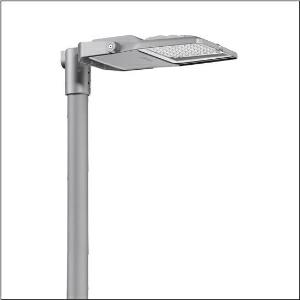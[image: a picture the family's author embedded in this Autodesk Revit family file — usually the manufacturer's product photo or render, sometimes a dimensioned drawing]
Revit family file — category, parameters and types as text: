
# Revit family: floodlight_fl_21_mini___pl33t_5xa7775d2f3a_2fb5
name_source: partatom
category: Lighting Fixtures
units: mm (PartAtom-declared; Revit-internal decimal feet)

## family parameters
Cut with Voids When Loaded = No
Host = Face
Light Source = No
Part Type = Normal
Room Calculation Point = No
Round Connector Dimension = Use Diameter
Shared = No

## types (1)
- --- (1 x LED, 17630 lm, 142.9 W, 3000K)
    Apparent Load = 143 VA
    CIE Flux Codes = 26 75 99 100 100
    Color Rendering = 70
    Color Temperature = 3000K
    Default Elevation = 1800 mm
    Description = Floodlight FL 21 mini, floodlight, primary light control with lens, of PMMA, primary optical cover: protective disc, of toughened safety glass, transparent, light distribution: PL33T, light emission: direct distribution, installation type: surface-mounted, LED, High Power LED, rated luminous flux: 17.630lm, luminous efficacy: 123lm/W, light colour: 730, colour temperature: 3000K, control: flexible luminous flux parameterisation, time-dependent luminous flux control, constant luminous flux control, overheat protection, presetting dimming logarithmic, with terminal, 6-pole, mains connection: 220..240V, AC, 50/60Hz, start of lifetime: 143W, end of service life: 151W, reduction: 63W, luminaire housing, of diecast aluminium, powder-coated, Siteco® metallic grey (DB 702S), corrosivity category C5 mid according to DIN EN ISO 12944, sealing non-destructively replaceable, please order mast flange separately, mast bracket, of steel, galvanised, powder-coated, Siteco® metallic grey (DB 702S), Smart Interface above, protection rating (complete): IP66, insulation class (complete): insulation class II (safety insulation), certification: CE, ENEC, VDE, protection symbol: D, impact resistance: IK08, permissible operating ambient temperature: -40..+40°C, permissible operating ambient temperature for outdoor applications: -40..+50°C, standard: DIN EN 12944, LABS conformity tested according to VDMA 24364:2018-05, packaging unit: 1 piece

Light Distribution: PL33T
    Height = 70 mm
    Lamp = 1 x LED
    Lamp Light Flux = 17630 lm
    Lamp Power = 142.9 W
    Lamp count = 1
    Length = 485 mm
    Luminous efficacy = 123 lm/W
    Manufacturer = Siteco
    ModVariant = No
    Model = 5XA7775D2F3A
    Number of Poles = 1
    OnlyDefault = Yes
    Power Factor = 1
    Product Name = Floodlight FL 21 mini | PL33T
    Product group = floodlight | pylon annexe
    ProductGroupID = 6200
    Protection Class = Protection class II
    Protection Degree = IP 66
    RLX_Detail_Level = 1
    RLX_Emergency_Light_Flux = 0 lm
    RLX_Emergency_Type = 0
    RLX_Emergency_Type_DB = No
    RlxData = <blob elided: 101141 chars, md5=ce09f7df>
    Socket = socket
    Standby Power = 0 W
    System Light Flux = 17630 lm
    System Power = 143 W
    Type Comments = factory setting: luminous flux: 100 % | dim-lin: 254 | 730 mA
    Type Image = l_1007125.jpg
    URL = http://relux.com
    VarID = @adj_080889
    Voltage = 0 V
    Weight = 0.00 kg
    Width = 337 mm

## geometry (parser evidence)
native form markers: Blend x4, Sweep x12
no freeform markers — native parametric forms only
